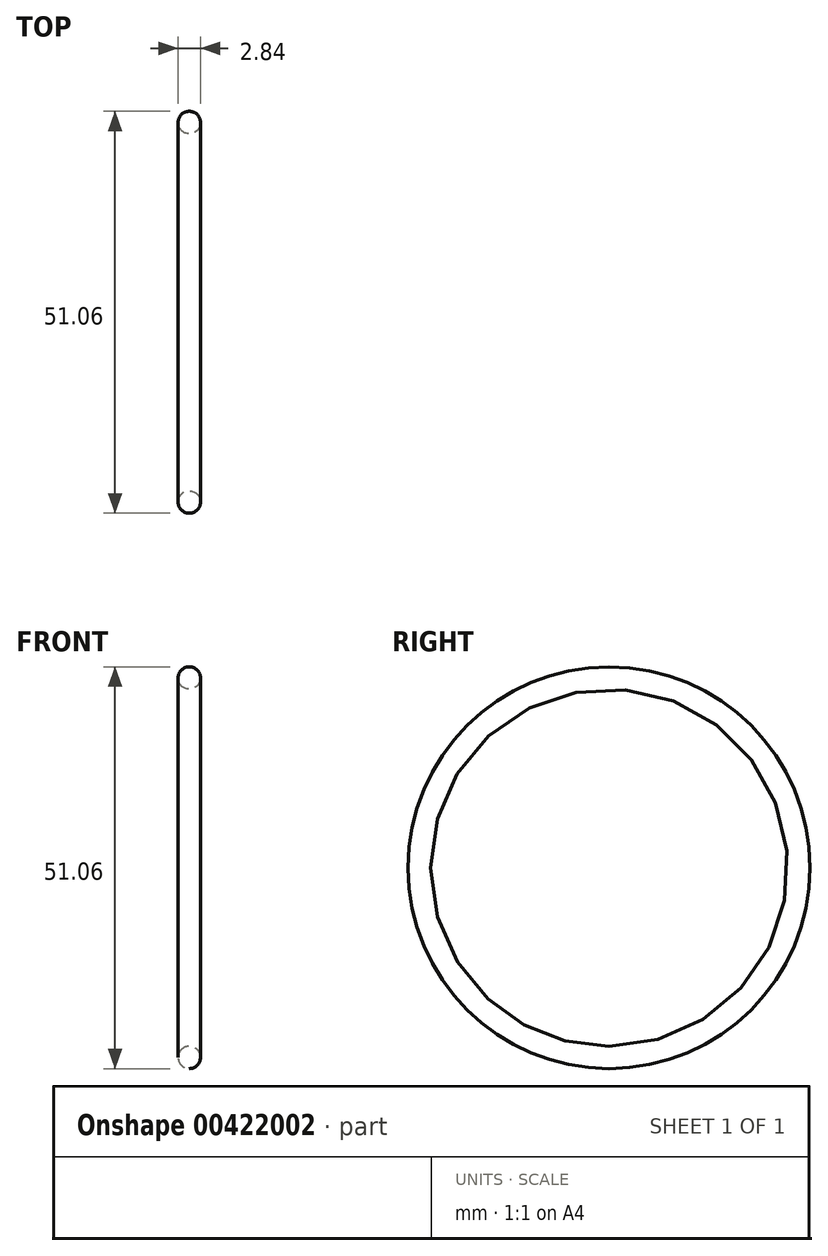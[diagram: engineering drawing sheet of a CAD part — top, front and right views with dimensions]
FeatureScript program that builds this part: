
annotation { "Feature Type Name" : "Feature", "Feature Type Description" : "" }
export const myFeature = defineFeature(function(context is Context, id is Id, definition is map)
    precondition{}
    {
        {
            var Q0;
            Q0=qCreatedBy(makeId("Right.planeOp"),FACE);
            var sketch = newSketch(context, id + "F0", { "sketchPlane" : qUnion([Q0])});
            skCircle(sketch, "E0", {"center": v(0, 0) * mm, "radius": 25.53 * mm});
            skSolve(sketch);
        }
        {
            var Q0;
            Q0=qCreatedBy(makeId("Top.planeOp"),FACE);
            var sketch = newSketch(context, id + "F1", { "sketchPlane" : qUnion([Q0])});
            skCircle(sketch, "E1", {"center": v(0, 24.1) * mm, "radius": 1.42 * mm});
            skSolve(sketch);
        }
        {
            var Q0;
            Q0=makeQuery(id+"F1.imprint","IMPRINT",FACE,{"disambiguationData":[TD([[makeQuery(id+"F1.imprint","IMPRINT",EDGE,{"derivedFrom":sQuery(id+"F1.wireOp",EDGE,"E1")}),1.0]])]});
            var Q1;
            Q1=sQuery(id+"F0.wireOp",EDGE,"E0");
            sweep(context, id + "F2", {"profiles" : qUnion([Q0]), "path" : qUnion([Q1])});
        }
    });
